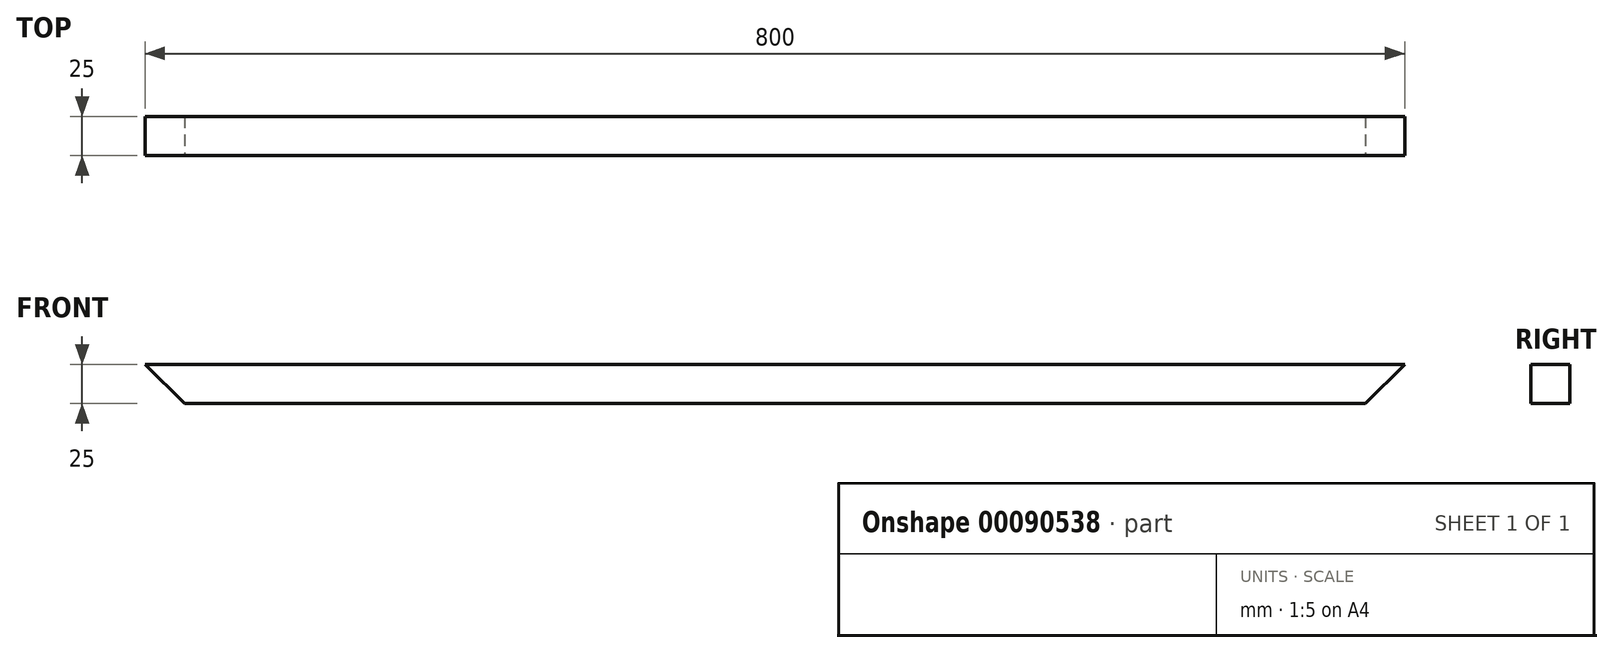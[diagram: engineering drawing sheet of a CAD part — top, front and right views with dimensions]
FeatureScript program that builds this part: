
annotation { "Feature Type Name" : "Feature", "Feature Type Description" : "" }
export const myFeature = defineFeature(function(context is Context, id is Id, definition is map)
    precondition{}
    {
        {
            var Q0;
            Q0=qCreatedBy(makeId("Right.planeOp"),FACE);
            var sketch = newSketch(context, id + "F0", { "sketchPlane" : qUnion([Q0])});
            skLineSegment(sketch, "E0.bottom", {"start": v(12.5, -12.5) * mm, "end": v(-12.5, -12.5) * mm});
            skLineSegment(sketch, "E0.top", {"start": v(12.5, 12.5) * mm, "end": v(-12.5, 12.5) * mm});
            skLineSegment(sketch, "E0.left", {"start": v(12.5, -12.5) * mm, "end": v(12.5, 12.5) * mm});
            skLineSegment(sketch, "E0.right", {"start": v(-12.5, -12.5) * mm, "end": v(-12.5, 12.5) * mm});
            skPoint(sketch, "E0.middle", {"position": v(0, 0) * mm});
            skSolve(sketch);
        }
        {
            var Q0;
            Q0 = qSketchRegion(id + "F0", true);
            extrude(context, id + "F1", {"entities" : qUnion([Q0]), "depth" : 800 * mm});
        }
        {
            var Q0;
            Q0=qCreatedBy(makeId("Front.planeOp"),FACE);
            var sketch = newSketch(context, id + "F2", { "sketchPlane" : qUnion([Q0])});
            skLineSegment(sketch, "E1", {"start": v(0, 12.5) * mm, "end": v(25, -12.5) * mm});
            skLineSegment(sketch, "E2", {"start": v(0, 12.5) * mm, "end": v(0, -12.5) * mm});
            skLineSegment(sketch, "E3", {"start": v(0, -12.5) * mm, "end": v(25, -12.5) * mm});
            skSolve(sketch);
        }
        {
            var Q0;
            Q0 = qSketchRegion(id + "F2", true);
            extrude(context, id + "F3", {"entities" : qUnion([Q0]), "operationType" : NewBodyOperationType.REMOVE, "endBound" : BoundingType.THROUGH_ALL, "oppositeDirection" : true, "depth" : 25 * mm, "hasSecondDirection" : true, "secondDirectionBound" : SecondDirectionBoundingType.THROUGH_ALL, "secondDirectionOppositeDirection" : false, "secondDirectionDepth" : 25 * mm});
        }
        {
            var Q0;
            Q0=qCreatedBy(makeId("Front.planeOp"),FACE);
            var sketch = newSketch(context, id + "F4", { "sketchPlane" : qUnion([Q0])});
            skLineSegment(sketch, "E4", {"start": v(800, 12.5) * mm, "end": v(775, -12.5) * mm});
            skLineSegment(sketch, "E5", {"start": v(775, -12.5) * mm, "end": v(800, -12.5) * mm});
            skLineSegment(sketch, "E6", {"start": v(800, -12.5) * mm, "end": v(800, 12.5) * mm});
            skSolve(sketch);
        }
        {
            var Q0;
            Q0 = qSketchRegion(id + "F4", true);
            extrude(context, id + "F5", {"entities" : qUnion([Q0]), "operationType" : NewBodyOperationType.REMOVE, "endBound" : BoundingType.THROUGH_ALL, "oppositeDirection" : true, "depth" : 25 * mm, "hasSecondDirection" : true, "secondDirectionBound" : SecondDirectionBoundingType.THROUGH_ALL, "secondDirectionOppositeDirection" : false, "secondDirectionDepth" : 25 * mm});
        }
    });
